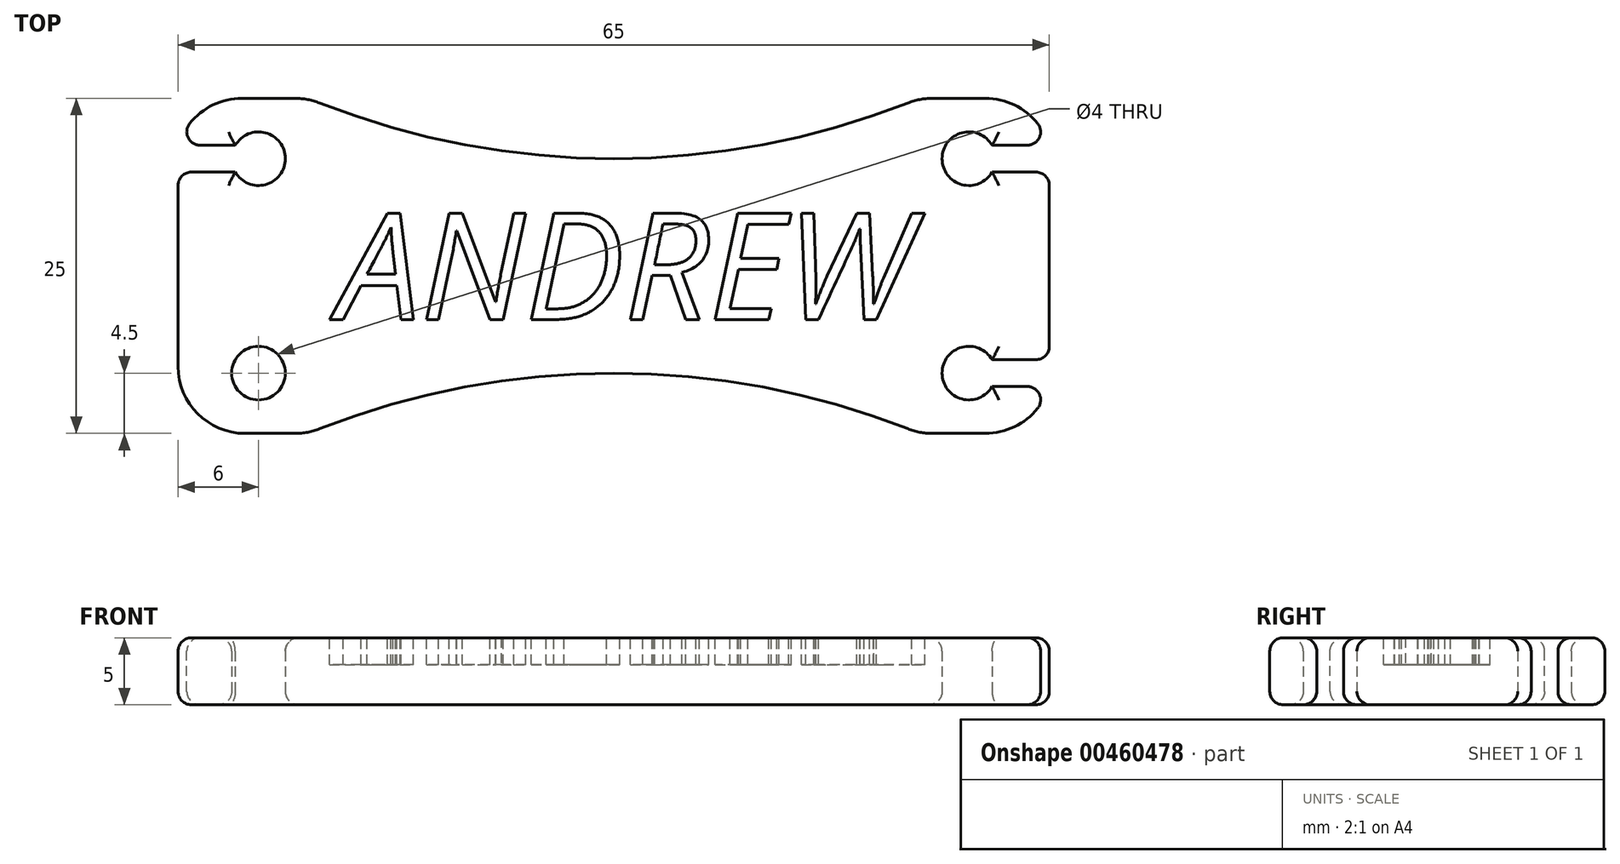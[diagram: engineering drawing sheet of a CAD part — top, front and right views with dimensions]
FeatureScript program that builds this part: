
annotation { "Feature Type Name" : "Feature", "Feature Type Description" : "" }
export const myFeature = defineFeature(function(context is Context, id is Id, definition is map)
    precondition{}
    {
        {
            var Q0;
            Q0=qCreatedBy(makeId("Top.planeOp"),FACE);
            var sketch = newSketch(context, id + "F0", { "sketchPlane" : qUnion([Q0])});
            skLineSegment(sketch, "E0.bottom", {"start": v(32.5, -12.5) * mm, "end": v(-32.5, -12.5) * mm});
            skLineSegment(sketch, "E0.top", {"start": v(32.5, 12.5) * mm, "end": v(-32.5, 12.5) * mm});
            skLineSegment(sketch, "E0.left", {"start": v(32.5, -12.5) * mm, "end": v(32.5, 12.5) * mm});
            skLineSegment(sketch, "E0.right", {"start": v(-32.5, -12.5) * mm, "end": v(-32.5, 12.5) * mm});
            skPoint(sketch, "E0.middle", {"position": v(0, 0) * mm});
            skSolve(sketch);
        }
        {
            var Q0;
            Q0 = qSketchRegion(id + "F0", true);
            extrude(context, id + "F1", {"entities" : qUnion([Q0]), "depth" : 5 * mm});
        }
        {
            var Q0;
            Q0=makeQuery(id+"F1.opExtrude","CAP_FACE",FACE,{"disambiguationData":[OSD([sQuery(id+"F0.wireOp",EDGE,"E0.bottom"),sQuery(id+"F0.wireOp",EDGE,"E0.top"),sQuery(id+"F0.wireOp",EDGE,"E0.left"),sQuery(id+"F0.wireOp",EDGE,"E0.right")])],"isStart":false});
            var sketch = newSketch(context, id + "F2", { "sketchPlane" : qUnion([Q0])});
            skCircle(sketch, "E1", {"center": v(0, 68) * mm, "radius": 60 * mm});
            skCircle(sketch, "E2.MirrorC", {"center": v(0, -68) * mm, "radius": 60 * mm});
            skSolve(sketch);
        }
        {
            var Q0;
            Q0 = qSketchRegion(id + "F2", true);
            extrude(context, id + "F3", {"entities" : qUnion([Q0]), "operationType" : NewBodyOperationType.REMOVE, "endBound" : BoundingType.THROUGH_ALL, "oppositeDirection" : true, "depth" : 25 * mm});
        }
        {
            var Q0;
            Q0=makeQuery(id+"F1.opExtrude","CAP_FACE",FACE,{"disambiguationData":[OSD([sQuery(id+"F0.wireOp",EDGE,"E0.bottom"),sQuery(id+"F0.wireOp",EDGE,"E0.top"),sQuery(id+"F0.wireOp",EDGE,"E0.left"),sQuery(id+"F0.wireOp",EDGE,"E0.right")])],"isStart":false});
            var sketch = newSketch(context, id + "F4", { "sketchPlane" : qUnion([Q0])});
            skCircle(sketch, "E3", {"center": v(26.5, 8) * mm, "radius": 2 * mm});
            skLineSegment(sketch, "E4.bottom", {"start": v(26.5, 9) * mm, "end": v(32.5, 9) * mm});
            skLineSegment(sketch, "E4.top", {"start": v(26.5, 7) * mm, "end": v(32.5, 7) * mm});
            skLineSegment(sketch, "E4.left", {"start": v(26.5, 9) * mm, "end": v(26.5, 7) * mm});
            skLineSegment(sketch, "E4.right", {"start": v(32.5, 9) * mm, "end": v(32.5, 7) * mm});
            skCircle(sketch, "E5.MirrorC", {"center": v(26.5, -8) * mm, "radius": 2 * mm});
            skLineSegment(sketch, "E6.MirrorCS", {"start": v(26.5, -9) * mm, "end": v(26.5, -7) * mm});
            skLineSegment(sketch, "E7.MirrorCS", {"start": v(26.5, -9) * mm, "end": v(32.5, -9) * mm});
            skLineSegment(sketch, "E8.MirrorCS", {"start": v(26.5, -7) * mm, "end": v(32.5, -7) * mm});
            skLineSegment(sketch, "E9.MirrorCS", {"start": v(32.5, -9) * mm, "end": v(32.5, -7) * mm});
            skCircle(sketch, "E10.MirrorC", {"center": v(-26.5, 8) * mm, "radius": 2 * mm});
            skLineSegment(sketch, "E11.MirrorCS", {"start": v(-26.5, 9) * mm, "end": v(-26.5, 7) * mm});
            skLineSegment(sketch, "E12.MirrorCS", {"start": v(-26.5, 7) * mm, "end": v(-32.5, 7) * mm});
            skLineSegment(sketch, "E13.MirrorCS", {"start": v(-26.5, 9) * mm, "end": v(-32.5, 9) * mm});
            skLineSegment(sketch, "E14.MirrorCS", {"start": v(-32.5, 9) * mm, "end": v(-32.5, 7) * mm});
            skCircle(sketch, "E15.MirrorC", {"center": v(-26.5, -8) * mm, "radius": 2 * mm});
            skSolve(sketch);
        }
        {
            var Q0;
            Q0 = qSketchRegion(id + "F4", true);
            extrude(context, id + "F5", {"entities" : qUnion([Q0]), "operationType" : NewBodyOperationType.REMOVE, "endBound" : BoundingType.THROUGH_ALL, "depth" : -5.4 * mm, "hasSecondDirection" : true, "secondDirectionOppositeDirection" : true, "secondDirectionDepth" : 25 * mm});
        }
        {
            var Q0;
            Q0=makeQuery(id+"F1.opExtrude","SWEPT_EDGE",EDGE,{"disambiguationData":[OSD([sQuery(id+"F0.wireOp",EDGE,"E0.bottom"),sQuery(id+"F0.wireOp",EDGE,"E0.left")])]});
            var Q1;
            Q1=makeQuery(id+"F1.opExtrude","SWEPT_EDGE",EDGE,{"disambiguationData":[OSD([sQuery(id+"F0.wireOp",EDGE,"E0.top"),sQuery(id+"F0.wireOp",EDGE,"E0.left")])]});
            var Q2;
            Q2=makeQuery(id+"F1.opExtrude","SWEPT_EDGE",EDGE,{"disambiguationData":[OSD([sQuery(id+"F0.wireOp",EDGE,"E0.bottom"),sQuery(id+"F0.wireOp",EDGE,"E0.right")])]});
            var Q3;
            Q3=makeQuery(id+"F1.opExtrude","SWEPT_EDGE",EDGE,{"disambiguationData":[OSD([sQuery(id+"F0.wireOp",EDGE,"E0.top"),sQuery(id+"F0.wireOp",EDGE,"E0.right")])]});
            fillet(context, id + "F6", {"entities" : qUnion([Q0, Q1, Q2, Q3]), "radius" : 5 * mm, "tangentPropagation" : true, "allowEdgeOverflow" : false});
        }
        {
            var Q0;
            Q0=makeQuery(id+"F3.boolean.opBoolean","INTERSECT",EDGE,{"disambiguationData":[OD(1.0)],"derivedFrom":[makeQuery(id+"F1.opExtrude","SWEPT_FACE",FACE,{"disambiguationData":[OSD([sQuery(id+"F0.wireOp",EDGE,"E0.bottom")])]}),makeQuery(id+"F3.opExtrude","SWEPT_FACE",FACE,{"disambiguationData":[OSD([sQuery(id+"F2.wireOp",EDGE,"E2.MirrorC")])]})]});
            var Q1;
            Q1=makeQuery(id+"F3.boolean.opBoolean","INTERSECT",EDGE,{"disambiguationData":[OD(0.0)],"derivedFrom":[makeQuery(id+"F1.opExtrude","SWEPT_FACE",FACE,{"disambiguationData":[OSD([sQuery(id+"F0.wireOp",EDGE,"E0.bottom")])]}),makeQuery(id+"F3.opExtrude","SWEPT_FACE",FACE,{"disambiguationData":[OSD([sQuery(id+"F2.wireOp",EDGE,"E2.MirrorC")])]})]});
            var Q2;
            Q2=makeQuery(id+"F3.boolean.opBoolean","INTERSECT",EDGE,{"disambiguationData":[OD(0.0)],"derivedFrom":[makeQuery(id+"F1.opExtrude","SWEPT_FACE",FACE,{"disambiguationData":[OSD([sQuery(id+"F0.wireOp",EDGE,"E0.top")])]}),makeQuery(id+"F3.opExtrude","SWEPT_FACE",FACE,{"disambiguationData":[OSD([sQuery(id+"F2.wireOp",EDGE,"E1")])]})]});
            var Q3;
            Q3=makeQuery(id+"F3.boolean.opBoolean","INTERSECT",EDGE,{"disambiguationData":[OD(1.0)],"derivedFrom":[makeQuery(id+"F1.opExtrude","SWEPT_FACE",FACE,{"disambiguationData":[OSD([sQuery(id+"F0.wireOp",EDGE,"E0.top")])]}),makeQuery(id+"F3.opExtrude","SWEPT_FACE",FACE,{"disambiguationData":[OSD([sQuery(id+"F2.wireOp",EDGE,"E1")])]})]});
            fillet(context, id + "F7", {"entities" : qUnion([Q0, Q1, Q2, Q3]), "radius" : 5 * mm, "tangentPropagation" : true, "allowEdgeOverflow" : false});
        }
        {
            var Q0;
            Q0=makeQuery(id+"F1.opExtrude","CAP_FACE",FACE,{"disambiguationData":[OSD([sQuery(id+"F0.wireOp",EDGE,"E0.bottom"),sQuery(id+"F0.wireOp",EDGE,"E0.top"),sQuery(id+"F0.wireOp",EDGE,"E0.left"),sQuery(id+"F0.wireOp",EDGE,"E0.right")])],"isStart":true});
            var Q1;
            Q1=makeQuery(id+"F1.opExtrude","CAP_FACE",FACE,{"disambiguationData":[OSD([sQuery(id+"F0.wireOp",EDGE,"E0.bottom"),sQuery(id+"F0.wireOp",EDGE,"E0.top"),sQuery(id+"F0.wireOp",EDGE,"E0.left"),sQuery(id+"F0.wireOp",EDGE,"E0.right")])],"isStart":false});
            var Q2;
            Q2=makeQuery(id+"F5.boolean.opBoolean","COPY",EDGE,{"derivedFrom":makeQuery(id+"F5.opExtrude","SWEPT_EDGE",EDGE,{"disambiguationData":[OSD([sQuery(id+"F0.wireOp",EDGE,"E0.left"),sQuery(id+"F4.wireOp",EDGE,"E4.top"),sQuery(id+"F4.wireOp",EDGE,"E4.right")])]})});
            var Q3;
            Q3=makeQuery(id+"F6.opFillet","BLEND_EDGE",EDGE,{"blendedFrom":[makeQuery(id+"F1.opExtrude","SWEPT_EDGE",EDGE,{"disambiguationData":[OSD([sQuery(id+"F0.wireOp",EDGE,"E0.top"),sQuery(id+"F0.wireOp",EDGE,"E0.left")])]}),makeQuery(id+"F5.boolean.opBoolean","COPY",FACE,{"derivedFrom":makeQuery(id+"F5.opExtrude","SWEPT_FACE",FACE,{"disambiguationData":[OSD([sQuery(id+"F4.wireOp",EDGE,"E4.bottom")])]})})],"blendedInto":[makeQuery(id+"F5.boolean.opBoolean","COPY",FACE,{"derivedFrom":makeQuery(id+"F5.opExtrude","SWEPT_FACE",FACE,{"disambiguationData":[OSD([sQuery(id+"F4.wireOp",EDGE,"E4.bottom")])]})})]});
            var Q4;
            Q4=makeQuery(id+"F5.boolean.opBoolean","COPY",EDGE,{"derivedFrom":makeQuery(id+"F5.opExtrude","SWEPT_EDGE",EDGE,{"disambiguationData":[OSD([sQuery(id+"F0.wireOp",EDGE,"E0.left"),sQuery(id+"F4.wireOp",EDGE,"E8.MirrorCS"),sQuery(id+"F4.wireOp",EDGE,"E9.MirrorCS")])]})});
            var Q5;
            Q5=makeQuery(id+"F6.opFillet","BLEND_EDGE",EDGE,{"blendedFrom":[makeQuery(id+"F1.opExtrude","SWEPT_EDGE",EDGE,{"disambiguationData":[OSD([sQuery(id+"F0.wireOp",EDGE,"E0.bottom"),sQuery(id+"F0.wireOp",EDGE,"E0.left")])]}),makeQuery(id+"F5.boolean.opBoolean","COPY",FACE,{"derivedFrom":makeQuery(id+"F5.opExtrude","SWEPT_FACE",FACE,{"disambiguationData":[OSD([sQuery(id+"F4.wireOp",EDGE,"E7.MirrorCS")])]})})],"blendedInto":[makeQuery(id+"F5.boolean.opBoolean","COPY",FACE,{"derivedFrom":makeQuery(id+"F5.opExtrude","SWEPT_FACE",FACE,{"disambiguationData":[OSD([sQuery(id+"F4.wireOp",EDGE,"E7.MirrorCS")])]})})]});
            var Q6;
            Q6=makeQuery(id+"F6.opFillet","BLEND_EDGE",EDGE,{"blendedFrom":[makeQuery(id+"F1.opExtrude","SWEPT_EDGE",EDGE,{"disambiguationData":[OSD([sQuery(id+"F0.wireOp",EDGE,"E0.top"),sQuery(id+"F0.wireOp",EDGE,"E0.right")])]}),makeQuery(id+"F5.boolean.opBoolean","COPY",FACE,{"derivedFrom":makeQuery(id+"F5.opExtrude","SWEPT_FACE",FACE,{"disambiguationData":[OSD([sQuery(id+"F4.wireOp",EDGE,"E13.MirrorCS")])]})})],"blendedInto":[makeQuery(id+"F5.boolean.opBoolean","COPY",FACE,{"derivedFrom":makeQuery(id+"F5.opExtrude","SWEPT_FACE",FACE,{"disambiguationData":[OSD([sQuery(id+"F4.wireOp",EDGE,"E13.MirrorCS")])]})})]});
            var Q7;
            Q7=makeQuery(id+"F5.boolean.opBoolean","COPY",EDGE,{"derivedFrom":makeQuery(id+"F5.opExtrude","SWEPT_EDGE",EDGE,{"disambiguationData":[OSD([sQuery(id+"F0.wireOp",EDGE,"E0.right"),sQuery(id+"F4.wireOp",EDGE,"E12.MirrorCS"),sQuery(id+"F4.wireOp",EDGE,"E14.MirrorCS")])]})});
            fillet(context, id + "F8", {"entities" : qUnion([Q0, Q1, Q2, Q3, Q4, Q5, Q6, Q7]), "radius" : 1 * mm, "tangentPropagation" : true, "allowEdgeOverflow" : false});
        }
        {
            var Q0;
            Q0=makeQuery(id+"F1.opExtrude","CAP_FACE",FACE,{"disambiguationData":[OSD([sQuery(id+"F0.wireOp",EDGE,"E0.bottom"),sQuery(id+"F0.wireOp",EDGE,"E0.top"),sQuery(id+"F0.wireOp",EDGE,"E0.left"),sQuery(id+"F0.wireOp",EDGE,"E0.right")])],"isStart":false});
            var sketch = newSketch(context, id + "F9", { "sketchPlane" : qUnion([Q0])});
            skText(sketch, "E16", { "text": "ANDREW\n", "fontName": "OpenSans-Italic.ttf"});
            const initialGuessF9  = {"E16": [-0.02058, -0.004, 1, 0, 0.008]};
            skSetInitialGuess(sketch, initialGuessF9);
            skSolve(sketch);
        }
        {
            var Q0;
            Q0 = qSketchRegion(id + "F9", true);
            extrude(context, id + "F10", {"entities" : qUnion([Q0]), "operationType" : NewBodyOperationType.REMOVE, "oppositeDirection" : true, "depth" : 2 * mm});
        }
    });
